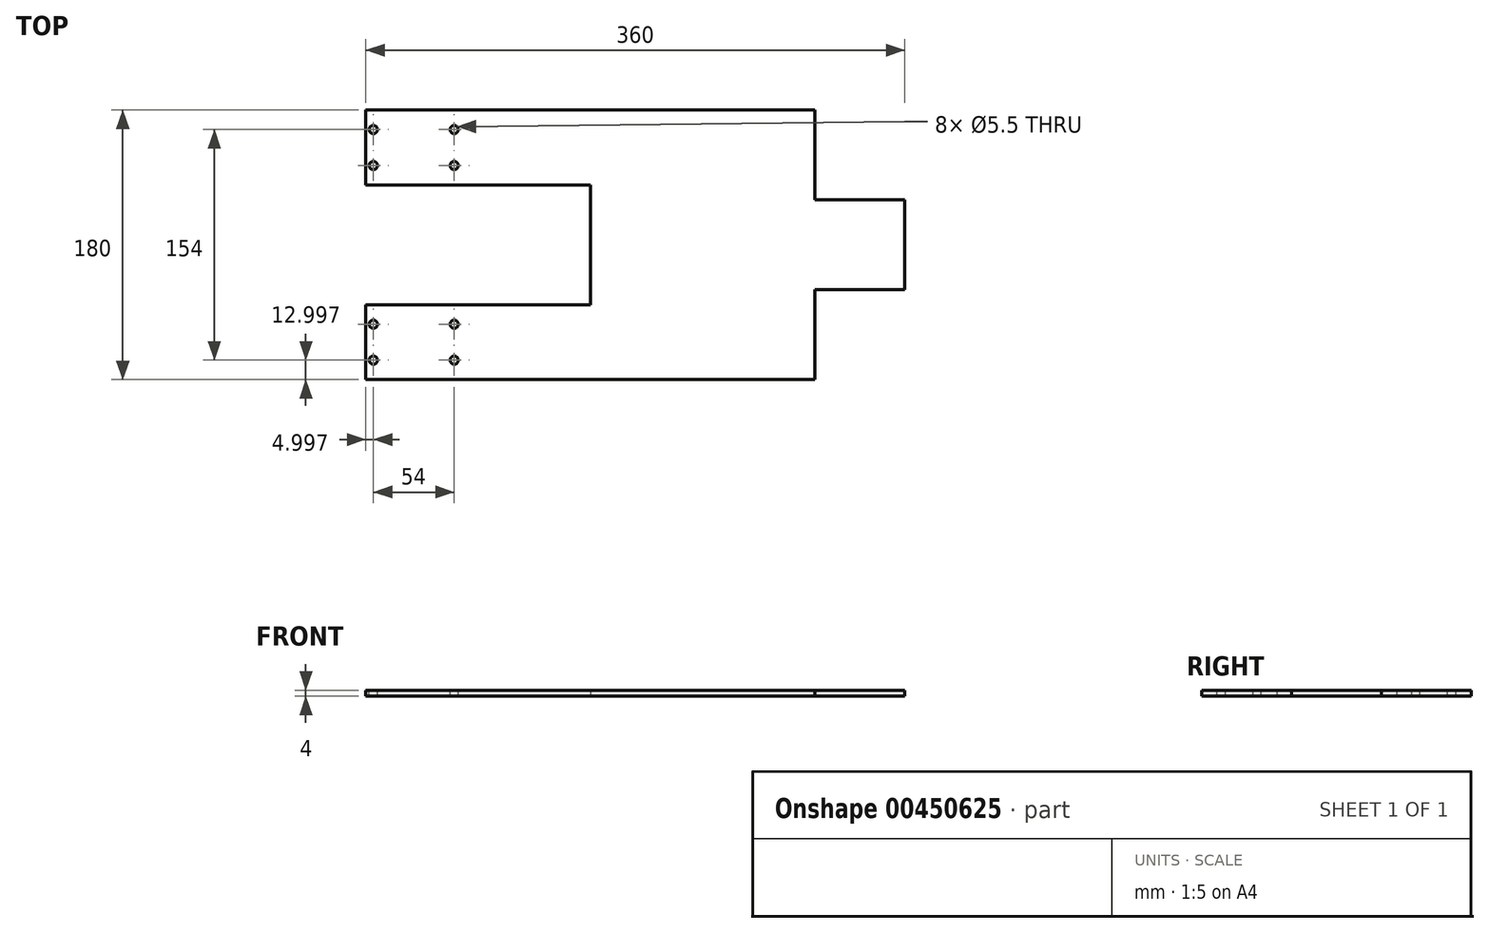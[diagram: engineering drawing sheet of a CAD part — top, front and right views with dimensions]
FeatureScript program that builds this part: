
annotation { "Feature Type Name" : "Feature", "Feature Type Description" : "" }
export const myFeature = defineFeature(function(context is Context, id is Id, definition is map)
    precondition{}
    {
        {
            var Q0;
            Q0=qCreatedBy(makeId("Top.planeOp"),FACE);
            var sketch = newSketch(context, id + "F0", { "sketchPlane" : qUnion([Q0])});
            skLineSegment(sketch, "E0", {"start": v(-124.56, 97.12) * mm, "end": v(-124.56, 47.12) * mm});
            skLineSegment(sketch, "E1", {"start": v(-124.56, 47.12) * mm, "end": v(25.44, 47.12) * mm});
            skLineSegment(sketch, "E2", {"start": v(25.44, 47.12) * mm, "end": v(25.44, -32.88) * mm});
            skLineSegment(sketch, "E3", {"start": v(25.44, -32.88) * mm, "end": v(-124.56, -32.88) * mm});
            skLineSegment(sketch, "E4", {"start": v(-124.56, -32.88) * mm, "end": v(-124.56, -82.88) * mm});
            skLineSegment(sketch, "E5", {"start": v(-124.56, -82.88) * mm, "end": v(175.44, -82.88) * mm});
            skLineSegment(sketch, "E6", {"start": v(175.44, -82.88) * mm, "end": v(175.44, -22.88) * mm});
            skLineSegment(sketch, "E7", {"start": v(175.44, -22.88) * mm, "end": v(235.44, -22.88) * mm});
            skLineSegment(sketch, "E8", {"start": v(235.44, -22.88) * mm, "end": v(235.44, 37.12) * mm});
            skLineSegment(sketch, "E9", {"start": v(235.44, 37.12) * mm, "end": v(175.44, 37.12) * mm});
            skLineSegment(sketch, "E10", {"start": v(175.44, 37.12) * mm, "end": v(175.44, 97.12) * mm});
            skLineSegment(sketch, "E11", {"start": v(175.44, 97.12) * mm, "end": v(-124.56, 97.12) * mm});
            skSolve(sketch);
        }
        {
            var Q0;
            Q0 = qSketchRegion(id + "F0", true);
            extrude(context, id + "F1", {"entities" : qUnion([Q0]), "depth" : 4 * mm});
        }
        {
            var Q0;
            Q0=makeQuery(id+"F1.opExtrude","CAP_FACE",FACE,{"disambiguationData":[OSD([sQuery(id+"F0.wireOp",EDGE,"E0"),sQuery(id+"F0.wireOp",EDGE,"E1"),sQuery(id+"F0.wireOp",EDGE,"E2"),sQuery(id+"F0.wireOp",EDGE,"E3"),sQuery(id+"F0.wireOp",EDGE,"E4"),sQuery(id+"F0.wireOp",EDGE,"E5"),sQuery(id+"F0.wireOp",EDGE,"E6"),sQuery(id+"F0.wireOp",EDGE,"E7"),sQuery(id+"F0.wireOp",EDGE,"E8"),sQuery(id+"F0.wireOp",EDGE,"E9"),sQuery(id+"F0.wireOp",EDGE,"E10"),sQuery(id+"F0.wireOp",EDGE,"E11")])],"isStart":false});
            var sketch = newSketch(context, id + "F2", { "sketchPlane" : qUnion([Q0])});
            skLineSegment(sketch, "E12", {"start": v(-180.3, 84.12) * mm, "end": v(72.89, 84.12) * mm, "construction": true});
            skLineSegment(sketch, "E13", {"start": v(-176.5, 60.12) * mm, "end": v(72.89, 60.12) * mm, "construction": true});
            skLineSegment(sketch, "E14", {"start": v(-176.5, -69.88) * mm, "end": v(72.89, -69.88) * mm, "construction": true});
            skLineSegment(sketch, "E15", {"start": v(-179.04, -45.88) * mm, "end": v(69.1, -45.88) * mm, "construction": true});
            skLineSegment(sketch, "E16", {"start": v(-119.56, 142.85) * mm, "end": v(-119.56, -136.93) * mm, "construction": true});
            skLineSegment(sketch, "E17", {"start": v(-65.56, 142.85) * mm, "end": v(-65.56, -136.93) * mm, "construction": true});
            skCircle(sketch, "E18", {"center": v(-119.56, 84.12) * mm, "radius": 2.75 * mm});
            skCircle(sketch, "E19", {"center": v(-65.56, 84.12) * mm, "radius": 2.75 * mm});
            skCircle(sketch, "E20", {"center": v(-65.56, 60.12) * mm, "radius": 2.75 * mm});
            skCircle(sketch, "E21", {"center": v(-119.56, 60.12) * mm, "radius": 2.75 * mm});
            skCircle(sketch, "E22", {"center": v(-119.56, -45.88) * mm, "radius": 2.75 * mm});
            skCircle(sketch, "E23", {"center": v(-119.56, -69.88) * mm, "radius": 2.75 * mm});
            skCircle(sketch, "E24", {"center": v(-65.56, -45.88) * mm, "radius": 2.75 * mm});
            skCircle(sketch, "E25", {"center": v(-65.56, -69.88) * mm, "radius": 2.75 * mm});
            skSolve(sketch);
        }
        {
            var Q0;
            Q0 = qSketchRegion(id + "F2", true);
            extrude(context, id + "F3", {"entities" : qUnion([Q0]), "operationType" : NewBodyOperationType.REMOVE, "oppositeDirection" : true, "depth" : 5 * mm});
        }
    });
